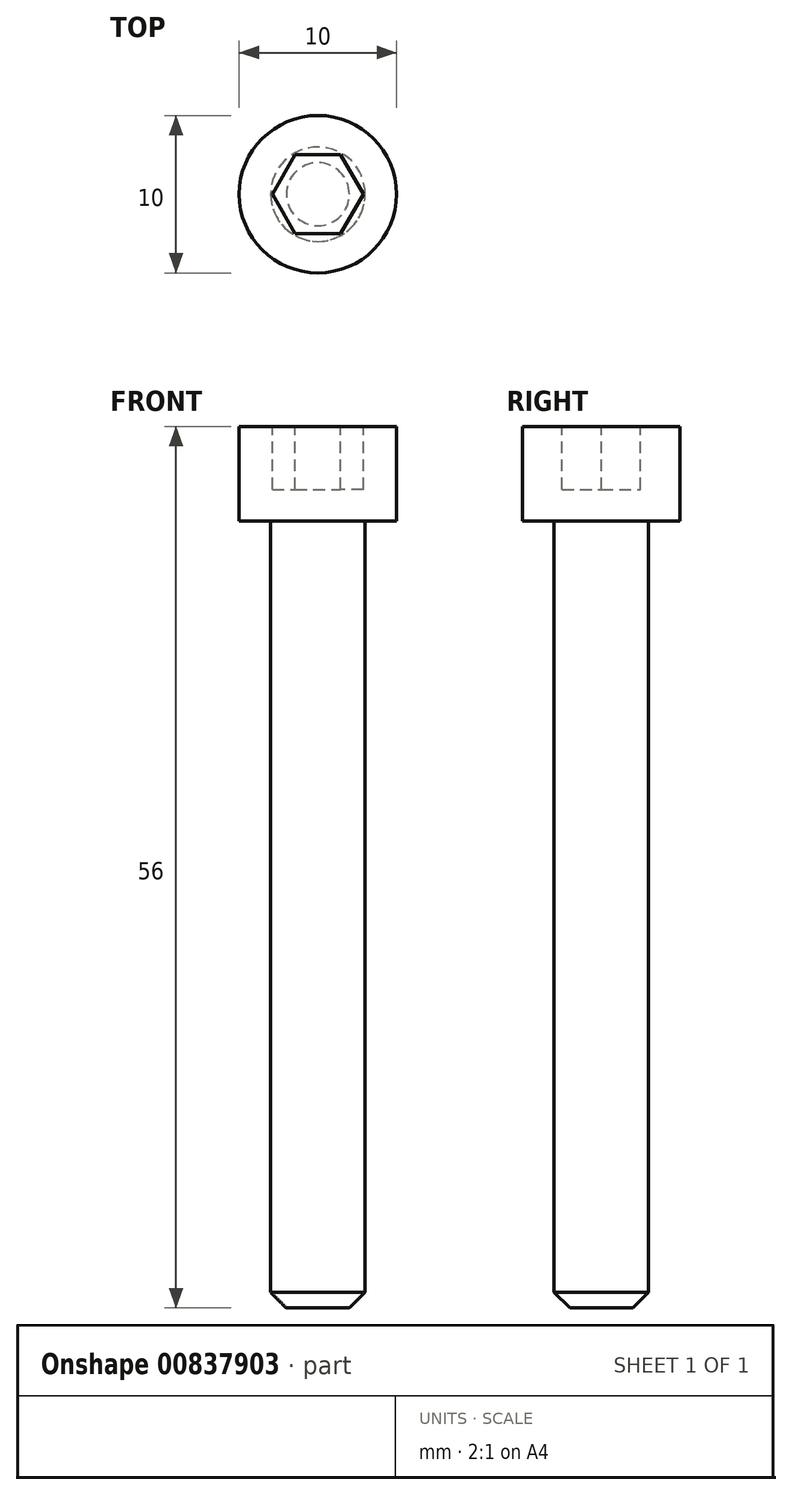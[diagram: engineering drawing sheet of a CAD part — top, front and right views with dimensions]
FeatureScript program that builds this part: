
annotation { "Feature Type Name" : "Feature", "Feature Type Description" : "" }
export const myFeature = defineFeature(function(context is Context, id is Id, definition is map)
    precondition{}
    {
        {
            var Q0;
            Q0=qCreatedBy(makeId("Front.planeOp"),FACE);
            var sketch = newSketch(context, id + "F0", { "sketchPlane" : qUnion([Q0])});
            skLineSegment(sketch, "E0", {"start": v(0, 6) * mm, "end": v(5, 6) * mm});
            skLineSegment(sketch, "E1", {"start": v(5, 6) * mm, "end": v(5, 0) * mm});
            skLineSegment(sketch, "E2", {"start": v(5, 0) * mm, "end": v(3, 0) * mm});
            skLineSegment(sketch, "E3", {"start": v(3, 0) * mm, "end": v(3, -50) * mm});
            skLineSegment(sketch, "E4", {"start": v(3, -50) * mm, "end": v(0, -50) * mm});
            skLineSegment(sketch, "E5", {"start": v(0, -50) * mm, "end": v(0, 6) * mm});
            skLineSegment(sketch, "E6", {"start": v(0, 32.65) * mm, "end": v(0, -133.76) * mm, "construction": true});
            skSolve(sketch);
        }
        {
            var Q0;
            Q0=makeQuery(id+"F0.imprint","IMPRINT",FACE,{"disambiguationData":[TD([[makeQuery(id+"F0.imprint","IMPRINT",EDGE,{"derivedFrom":sQuery(id+"F0.wireOp",EDGE,"E0")}),-1.0]])]});
            var Q1;
            Q1=sQuery(id+"F0.wireOp",EDGE,"E6");
            var Q2;
            Q2=sQuery(id+"F0.wireOp",EDGE,"E6");
            revolve(context, id + "F1", {"surfaceOperationType" : NewSurfaceOperationType.NEW, "entities" : qUnion([Q0]), "surfaceEntities" : qUnion([Q1]), "axis" : qUnion([Q2]), "revolveType" : RevolveType.FULL});
        }
        {
            var Q0;
            Q0=makeQuery(id+"F1.opRevolve","SWEPT_FACE",FACE,{"disambiguationData":[OSD([sQuery(id+"F0.wireOp",EDGE,"E0")])]});
            var sketch = newSketch(context, id + "F2", { "sketchPlane" : qUnion([Q0])});
            skCircle(sketch, "E7.cCircle", {"center": v(0, 0) * mm, "radius": 2.5 * mm, "construction": true});
            skLineSegment(sketch, "E7.0", {"start": v(-1.44, 2.5) * mm, "end": v(1.44, 2.5) * mm});
            skLineSegment(sketch, "E7.1", {"start": v(1.44, 2.5) * mm, "end": v(2.89, 0) * mm});
            skLineSegment(sketch, "E7.2", {"start": v(2.89, 0) * mm, "end": v(1.44, -2.5) * mm});
            skLineSegment(sketch, "E7.3", {"start": v(1.44, -2.5) * mm, "end": v(-1.44, -2.5) * mm});
            skLineSegment(sketch, "E7.4", {"start": v(-1.44, -2.5) * mm, "end": v(-2.89, 0) * mm});
            skLineSegment(sketch, "E7.5", {"start": v(-2.89, 0) * mm, "end": v(-1.44, 2.5) * mm});
            skPoint(sketch, "E7.0.midPoint", {"position": v(0, 2.5) * mm});
            skSolve(sketch);
        }
        {
            var Q0;
            Q0=qSketchRegion(id+"F2",true);
            extrude(context, id + "F3", {"entities" : qUnion([Q0]), "operationType" : NewBodyOperationType.REMOVE, "oppositeDirection" : true, "depth" : 4 * mm, "offsetDistance" : 25 * mm});
        }
        {
            var Q0;
            Q0=makeQuery(id+"F1.opRevolve","SWEPT_EDGE",EDGE,{"disambiguationData":[OSD([sQuery(id+"F0.wireOp",EDGE,"E3"),sQuery(id+"F0.wireOp",EDGE,"E4")])]});
            chamfer(context, id + "F4", {"entities" : qUnion([Q0]), "width" : 1 * mm, "tangentPropagation" : true});
        }
    });
